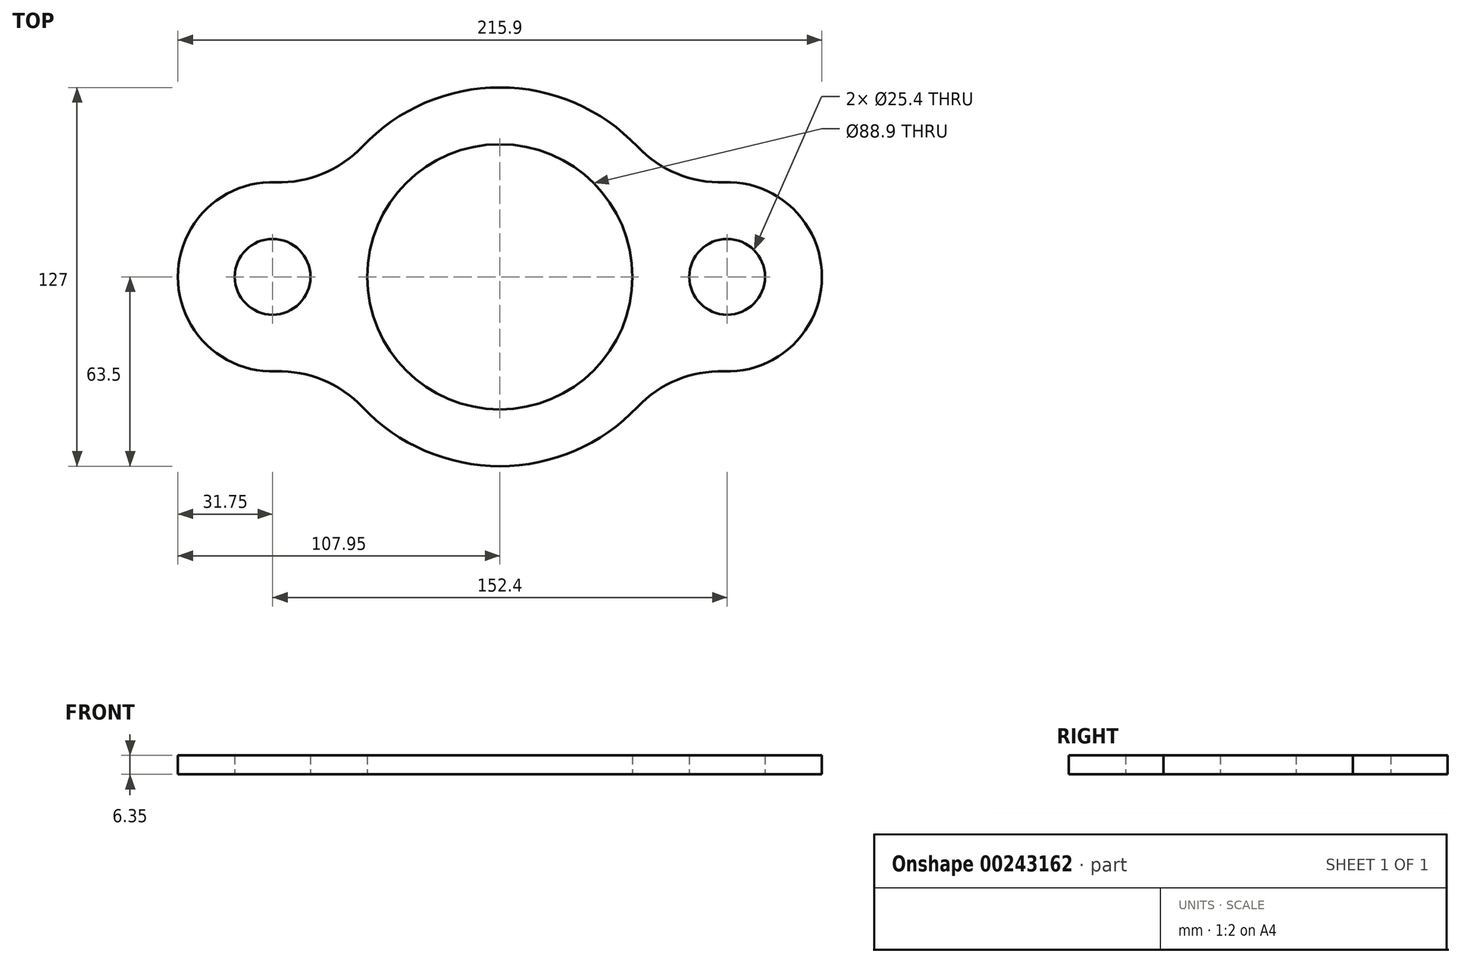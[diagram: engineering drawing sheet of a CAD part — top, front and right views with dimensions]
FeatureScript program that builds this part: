
annotation { "Feature Type Name" : "Feature", "Feature Type Description" : "" }
export const myFeature = defineFeature(function(context is Context, id is Id, definition is map)
    precondition{}
    {
        {
            var Q0;
            Q0=qCreatedBy(makeId("Top.planeOp"),FACE);
            var sketch = newSketch(context, id + "F0", { "sketchPlane" : qUnion([Q0])});
            skCircle(sketch, "E0", {"center": v(0, 0) * mm, "radius": 44.45 * mm});
            skArc(sketch, "E1", {"start": v(-46.14, -43.63) * mm, "mid": v(0, -63.5) * mm, "end": v(46.14, -43.63) * mm});
            skCircle(sketch, "E2", {"center": v(-76.2, 0) * mm, "radius": 12.7 * mm});
            skCircle(sketch, "E3", {"center": v(76.2, 0) * mm, "radius": 12.7 * mm});
            skArc(sketch, "E4", {"start": v(75.12, -31.73) * mm, "mid": v(107.95, 0) * mm, "end": v(75.12, 31.73) * mm});
            skArc(sketch, "E5", {"start": v(-75.12, 31.73) * mm, "mid": v(-107.95, 0) * mm, "end": v(-75.12, -31.73) * mm});
            skArc(sketch, "E6.trimOffspring", {"start": v(46.14, 43.63) * mm, "mid": v(0, 63.5) * mm, "end": v(-46.14, 43.63) * mm});
            skPoint(sketch, "E7.visualSharp", {"position": v(-57.94, 25.98) * mm});
            skArc(sketch, "E7.filletArc", {"start": v(-75.12, 31.73) * mm, "mid": v(-59.35, 34.56) * mm, "end": v(-46.14, 43.63) * mm});
            skPoint(sketch, "E8.visualSharp", {"position": v(-57.94, -25.98) * mm});
            skArc(sketch, "E8.filletArc", {"start": v(-46.14, -43.63) * mm, "mid": v(-59.35, -34.56) * mm, "end": v(-75.12, -31.73) * mm});
            skPoint(sketch, "E9.visualSharp", {"position": v(57.94, -25.98) * mm});
            skArc(sketch, "E9.filletArc", {"start": v(75.12, -31.73) * mm, "mid": v(59.35, -34.56) * mm, "end": v(46.14, -43.63) * mm});
            skPoint(sketch, "E10.visualSharp", {"position": v(57.94, 25.98) * mm});
            skArc(sketch, "E10.filletArc", {"start": v(46.14, 43.63) * mm, "mid": v(59.35, 34.56) * mm, "end": v(75.12, 31.73) * mm});
            skSolve(sketch);
        }
        {
            var Q0;
            Q0=makeQuery(id+"F0.imprint","IMPRINT",FACE,{"disambiguationData":[TD([[makeQuery(id+"F0.imprint","IMPRINT",EDGE,{"derivedFrom":sQuery(id+"F0.wireOp",EDGE,"E0")}),-1.0]])]});
            extrude(context, id + "F1", {"entities" : qUnion([Q0]), "depth" : 6.35 * mm});
        }
    });
